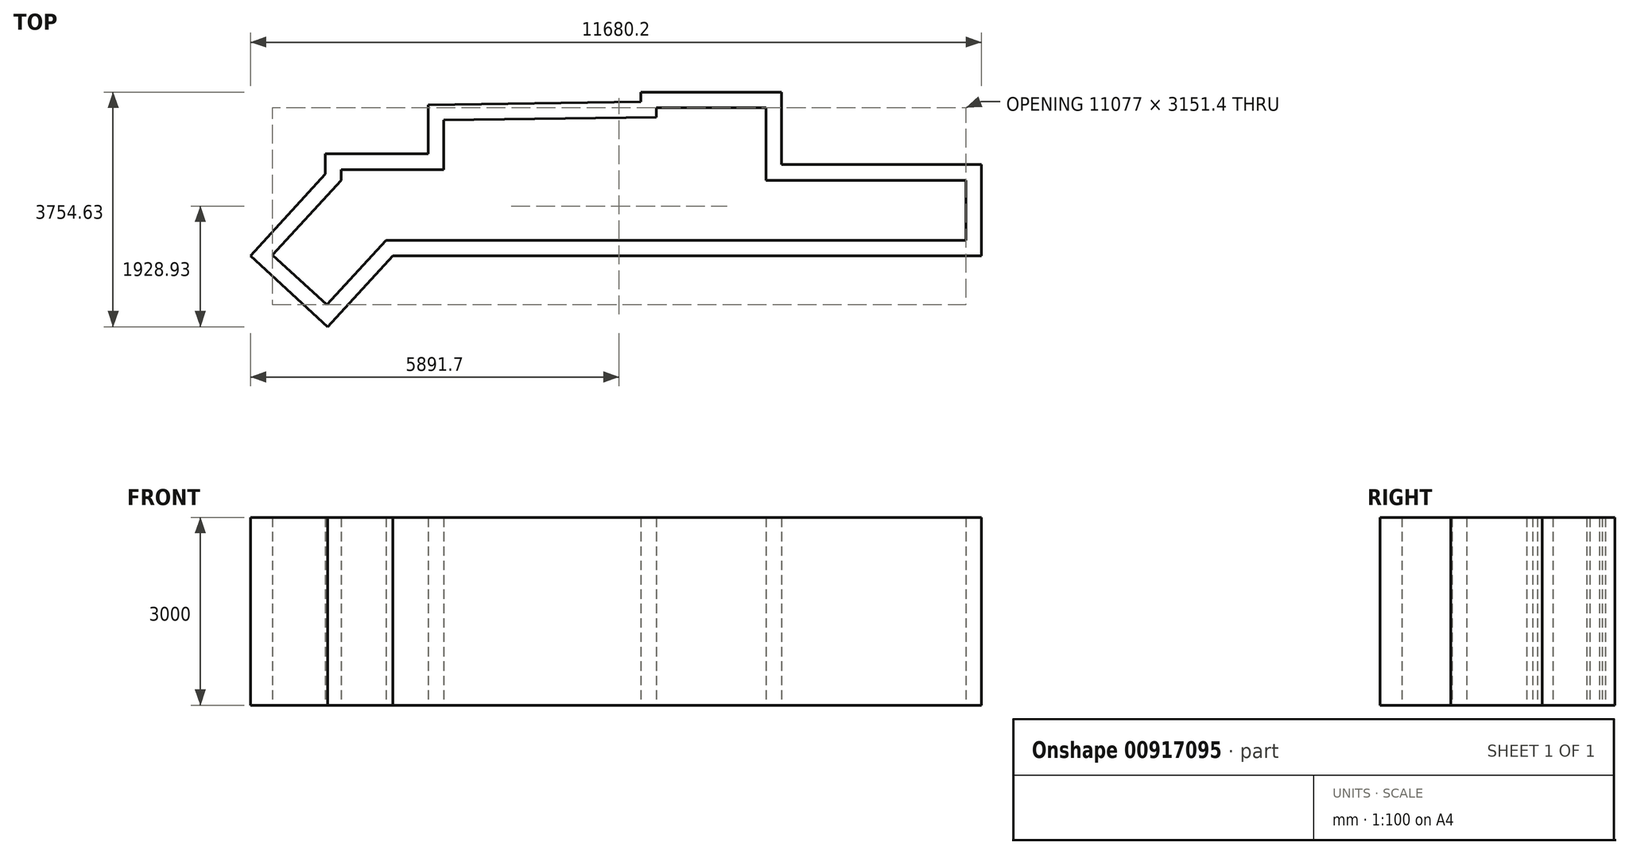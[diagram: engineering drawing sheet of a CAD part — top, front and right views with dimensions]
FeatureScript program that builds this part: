
annotation { "Feature Type Name" : "Feature", "Feature Type Description" : "" }
export const myFeature = defineFeature(function(context is Context, id is Id, definition is map)
    precondition{}
    {
        {
            var Q0;
            Q0=qCreatedBy(makeId("Top.planeOp"),FACE);
            var sketch = newSketch(context, id + "F0", { "sketchPlane" : qUnion([Q0])});
            skLineSegment(sketch, "E0", {"start": v(3038.66, -4461.27) * mm, "end": v(3038.66, -5621.27) * mm});
            skLineSegment(sketch, "E1", {"start": v(3038.66, -5621.27) * mm, "end": v(6230.53, -5621.27) * mm});
            skLineSegment(sketch, "E2", {"start": v(6230.53, -5621.27) * mm, "end": v(6230.53, -6581.27) * mm});
            skLineSegment(sketch, "E3", {"start": v(-2110.97, -4661.27) * mm, "end": v(-2110.97, -5451.27) * mm});
            skLineSegment(sketch, "E4", {"start": v(-2110.97, -5451.27) * mm, "end": v(-3750.97, -5451.27) * mm});
            skLineSegment(sketch, "E5", {"start": v(-3750.97, -5451.27) * mm, "end": v(-3750.97, -5621.27) * mm});
            skLineSegment(sketch, "E6", {"start": v(-3750.97, -5621.27) * mm, "end": v(-4846.42, -6814.74) * mm});
            skLineSegment(sketch, "E7", {"start": v(-4846.42, -6814.74) * mm, "end": v(-3977.1, -7612.67) * mm});
            skLineSegment(sketch, "E8", {"start": v(-3977.1, -7612.67) * mm, "end": v(-3030.41, -6581.27) * mm});
            skLineSegment(sketch, "E9", {"start": v(-3030.41, -6581.27) * mm, "end": v(6230.53, -6581.27) * mm});
            skLineSegment(sketch, "E10", {"start": v(3038.66, -4461.27) * mm, "end": v(1288.66, -4461.27) * mm});
            skLineSegment(sketch, "E11", {"start": v(1288.66, -4461.27) * mm, "end": v(1288.66, -4611.27) * mm});
            skLineSegment(sketch, "E12", {"start": v(1288.66, -4611.27) * mm, "end": v(-2110.97, -4661.27) * mm});
            skLineSegment(sketch, "E13.0", {"start": v(3288.66, -5371.27) * mm, "end": v(6480.53, -5371.27) * mm});
            skLineSegment(sketch, "E13.1", {"start": v(3288.66, -4211.27) * mm, "end": v(3288.66, -5371.27) * mm});
            skLineSegment(sketch, "E13.2", {"start": v(-4000.97, -5523.93) * mm, "end": v(-5199.65, -6829.87) * mm});
            skLineSegment(sketch, "E13.3", {"start": v(-5199.65, -6829.87) * mm, "end": v(-3961.98, -7965.9) * mm});
            skLineSegment(sketch, "E13.4", {"start": v(-3961.98, -7965.9) * mm, "end": v(-2920.54, -6831.27) * mm});
            skLineSegment(sketch, "E13.5", {"start": v(-2920.54, -6831.27) * mm, "end": v(6480.53, -6831.27) * mm});
            skLineSegment(sketch, "E13.6", {"start": v(-4000.97, -5201.27) * mm, "end": v(-4000.97, -5523.93) * mm});
            skLineSegment(sketch, "E13.7", {"start": v(-2360.97, -5201.27) * mm, "end": v(-4000.97, -5201.27) * mm});
            skLineSegment(sketch, "E13.8", {"start": v(6480.53, -5371.27) * mm, "end": v(6480.53, -6831.27) * mm});
            skLineSegment(sketch, "E13.9", {"start": v(-2360.97, -4414.92) * mm, "end": v(-2360.97, -5201.27) * mm});
            skLineSegment(sketch, "E13.10", {"start": v(1038.66, -4364.92) * mm, "end": v(-2360.97, -4414.92) * mm});
            skLineSegment(sketch, "E13.11", {"start": v(1038.66, -4211.27) * mm, "end": v(1038.66, -4364.92) * mm});
            skLineSegment(sketch, "E13.12", {"start": v(3288.66, -4211.27) * mm, "end": v(1038.66, -4211.27) * mm});
            skLineSegment(sketch, "E14.3.5.0", {"start": v(1180.67, -4612.86) * mm, "end": v(1216.67, -4612.33) * mm});
            skLineSegment(sketch, "E14.3.6.0", {"start": v(1252.67, -4611.8) * mm, "end": v(1288.66, -4611.27) * mm});
            skSolve(sketch);
        }
        {
            var Q0;
            Q0=makeQuery(id+"F0.imprint","IMPRINT",FACE,{"disambiguationData":[TD([[makeQuery(id+"F0.imprint","IMPRINT",EDGE,{"derivedFrom":sQuery(id+"F0.wireOp",EDGE,"E0")}),1.0]])]});
            extrude(context, id + "F1", {"entities" : qUnion([Q0]), "flatOperationType" : FlatOperationType.REMOVE, "depth" : 3000 * mm, "offsetDistance" : 25 * mm, "domain" : OperationDomain.MODEL});
        }
    });
